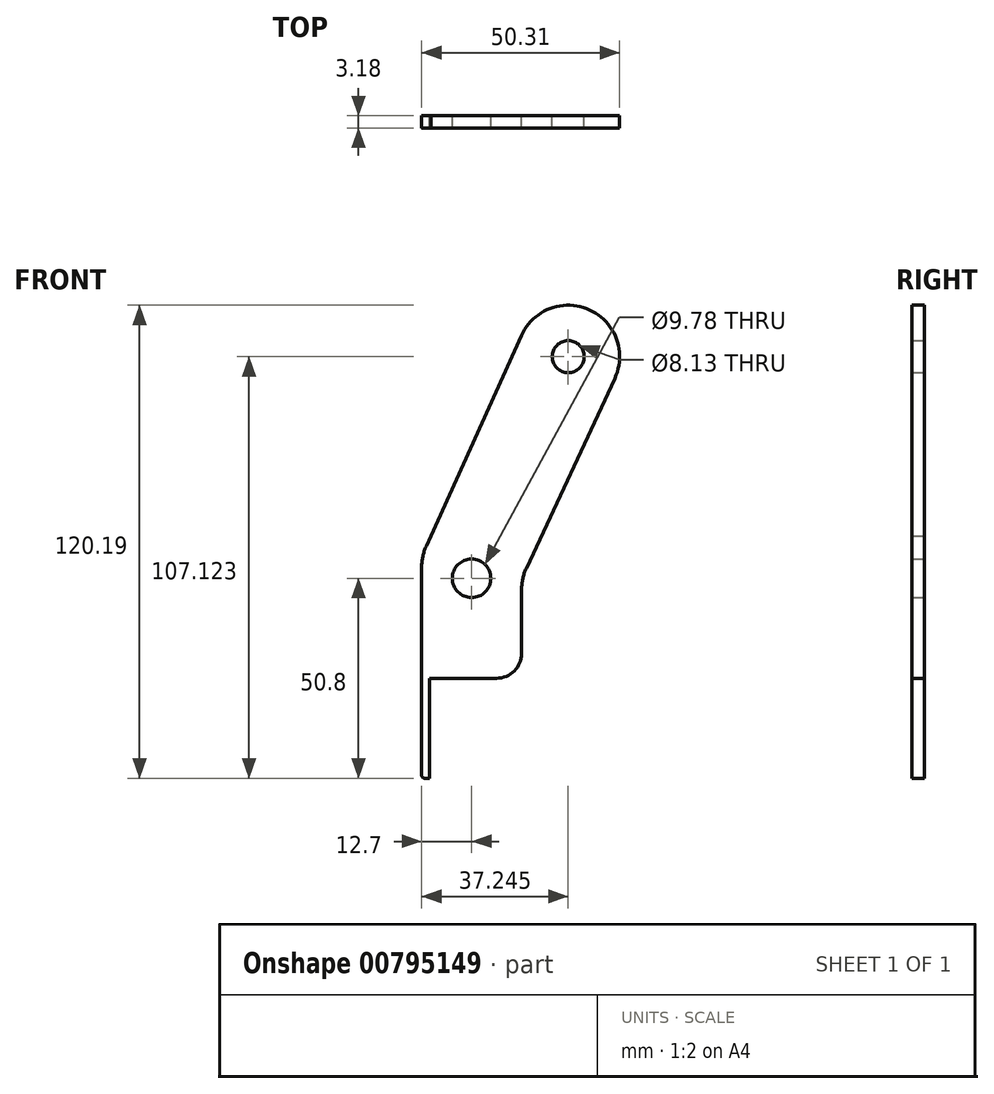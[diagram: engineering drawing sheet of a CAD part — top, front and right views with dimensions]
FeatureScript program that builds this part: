
annotation { "Feature Type Name" : "Feature", "Feature Type Description" : "" }
export const myFeature = defineFeature(function(context is Context, id is Id, definition is map)
    precondition{}
    {
        {
            var Q0;
            Q0=qCreatedBy(makeId("Front.planeOp"),FACE);
            var sketch = newSketch(context, id + "F0", { "sketchPlane" : qUnion([Q0])});
            skLineSegment(sketch, "E0.bottom", {"start": v(-10.67, -63.5) * mm, "end": v(-11.9, -63.5) * mm});
            skLineSegment(sketch, "E0.top", {"start": v(0, 63.5) * mm, "end": v(0, 63.5) * mm});
            skLineSegment(sketch, "E0.left", {"start": v(12.7, -31.75) * mm, "end": v(12.7, -15.52) * mm});
            skLineSegment(sketch, "E0.right", {"start": v(-12.7, -62.7) * mm, "end": v(-12.7, -13.23) * mm});
            skPoint(sketch, "E0.middle", {"position": v(0, 0) * mm});
            skCircle(sketch, "E1", {"center": v(0, -12.7) * mm, "radius": 4.89 * mm});
            skLineSegment(sketch, "E2", {"start": v(6.35, -38.1) * mm, "end": v(-10.67, -38.1) * mm});
            skLineSegment(sketch, "E3", {"start": v(-10.67, -38.1) * mm, "end": v(-10.67, -63.5) * mm});
            skPoint(sketch, "E4.visualSharp", {"position": v(-12.7, 63.5) * mm});
            skPoint(sketch, "E5.visualSharp", {"position": v(12.7, 63.5) * mm});
            skPoint(sketch, "E6.orphan", {"position": v(12.7, -63.5) * mm});
            skPoint(sketch, "E7.visualSharp", {"position": v(-12.7, -63.5) * mm});
            skArc(sketch, "E7.filletArc", {"start": v(-12.7, -62.7) * mm, "mid": v(-12.47, -63.27) * mm, "end": v(-11.9, -63.5) * mm});
            skPoint(sketch, "E8.visualSharp", {"position": v(12.7, -38.1) * mm});
            skArc(sketch, "E8.filletArc", {"start": v(6.35, -38.1) * mm, "mid": v(10.84, -36.24) * mm, "end": v(12.7, -31.75) * mm});
            skPoint(sketch, "E9.end.orphan", {"position": v(50.8, 45.96) * mm});
            skPoint(sketch, "E10.orphan", {"position": v(12.7, -20.03) * mm});
            skLineSegment(sketch, "E11", {"start": v(-12.7, -13.23) * mm, "end": v(-12.7, -9.88) * mm});
            skLineSegment(sketch, "E12", {"start": v(13.89, -10.15) * mm, "end": v(36.39, 38.1) * mm});
            skLineSegment(sketch, "E13", {"start": v(-10.32, -1.97) * mm, "end": v(-11.51, -4.52) * mm});
            skPoint(sketch, "E14.orphan", {"position": v(-12.7, -5.37) * mm});
            skPoint(sketch, "E15.center.orphan", {"position": v(0, 50.8) * mm});
            skArc(sketch, "E16", {"start": v(36.39, 38.1) * mm, "mid": v(29.99, 55.5) * mm, "end": v(12.63, 48.99) * mm});
            skCircle(sketch, "E17", {"center": v(24.54, 43.62) * mm, "radius": 4.06 * mm});
            skPoint(sketch, "E18.visualSharp", {"position": v(-12.7, -7.07) * mm});
            skArc(sketch, "E18.filletArc", {"start": v(-11.51, -4.52) * mm, "mid": v(-12.4, -7.14) * mm, "end": v(-12.7, -9.88) * mm});
            skPoint(sketch, "E19.visualSharp", {"position": v(12.7, -12.7) * mm});
            skArc(sketch, "E19.filletArc", {"start": v(13.89, -10.15) * mm, "mid": v(13, -12.77) * mm, "end": v(12.7, -15.52) * mm});
            skLineSegment(sketch, "E20", {"start": v(-10.32, -1.97) * mm, "end": v(12.63, 48.99) * mm});
            skSolve(sketch);
        }
        {
            var Q0;
            Q0=makeQuery(id+"F0.imprint","IMPRINT",FACE,{"disambiguationData":[TD([[makeQuery(id+"F0.imprint","IMPRINT",EDGE,{"derivedFrom":sQuery(id+"F0.wireOp",EDGE,"E0.bottom")}),-1.0]])]});
            extrude(context, id + "F1", {"entities" : qUnion([Q0]), "depth" : 3.17 * mm, "offsetDistance" : 25.4 * mm});
        }
    });
